# Revit family: HS 12, 18, 24
name_source: partatom
category: Windows
revit_build: Autodesk Revit LT 2016 (Build: 20150220_1215(x64)
units: mm (PartAtom-declared; Revit-internal decimal feet)

## family parameters
Always vertical = Yes
Cut with Voids When Loaded = No
Host = Wall
OmniClass Number = 23.30.20.00
OmniClass Title = Windows
Room Calculation Point = No
Shared = No

## types (12) — shared parameters
Aluminium = Aluminium
Default Sill Height = 914 mm
Glass = Glass
Manufacturer = Robmeg
Putty width = 5 mm  [stored 0.0164042 ft]
URL = http://www.robmeg.co.za
Wall Closure = By host

## per-type parameters (varying)
| type | Description | Height | Model | Width |
| HS1206 | Anodised Aluminium horizontal sliding window | 600 mm | HS1206 | 1200 mm |
| HS1209 | Anodised Aluminium Horizontal sliding window | 900 mm  [stored 2.95276 ft] | HS1029 | 1200 mm |
| HS1212 | Anodised Aluminium horizintal sliding window | 1200 mm | HS1212 | 1200 mm |
| HS1215 | Anodised Aluminium horizontal sliding window | 1500 mm  [stored 4.92126 ft] | HS1215 | 1200 mm |
| HS1806 | Anodised Aluminium Horizontal sliding window | 600 mm | HS1806 | 1800 mm  [stored 5.90551 ft] |
| HS1809 | Anodized Aluminium horizontal sliding window | 900 mm  [stored 2.95276 ft] | HS1809 | 1800 mm  [stored 5.90551 ft] |
| HS1812 | Anodised Aluminium horizontal sliding window | 1200 mm | HS1812 | 1800 mm  [stored 5.90551 ft] |
| HS1815 | Anodized aluminium horizontal sliding window | 1500 mm  [stored 4.92126 ft] | HS1815 | 1800 mm  [stored 5.90551 ft] |
| HS2406 | Andodised aluminium horizontal sliding window | 600 mm | HS2406 | 2400 mm |
| HS2409 | Anodised aluminium horizontal sliding window | 900 mm  [stored 2.95276 ft] | HS2409 | 2400 mm |
| HS2412 | Anodised aluminium Horizontal sliding window | 1200 mm | HS2412 | 2400 mm |
| HS2415 | Anodised aluminium horizontal sliding windows | 1500 mm  [stored 4.92126 ft] | HS2415 | 2400 mm |

note: [stored X ft] marks values corroborated as IEEE doubles in the binary element streams (Revit-internal decimal feet)

## geometry (parser evidence)
native form markers: Sweep x5
no freeform markers — native parametric forms only
